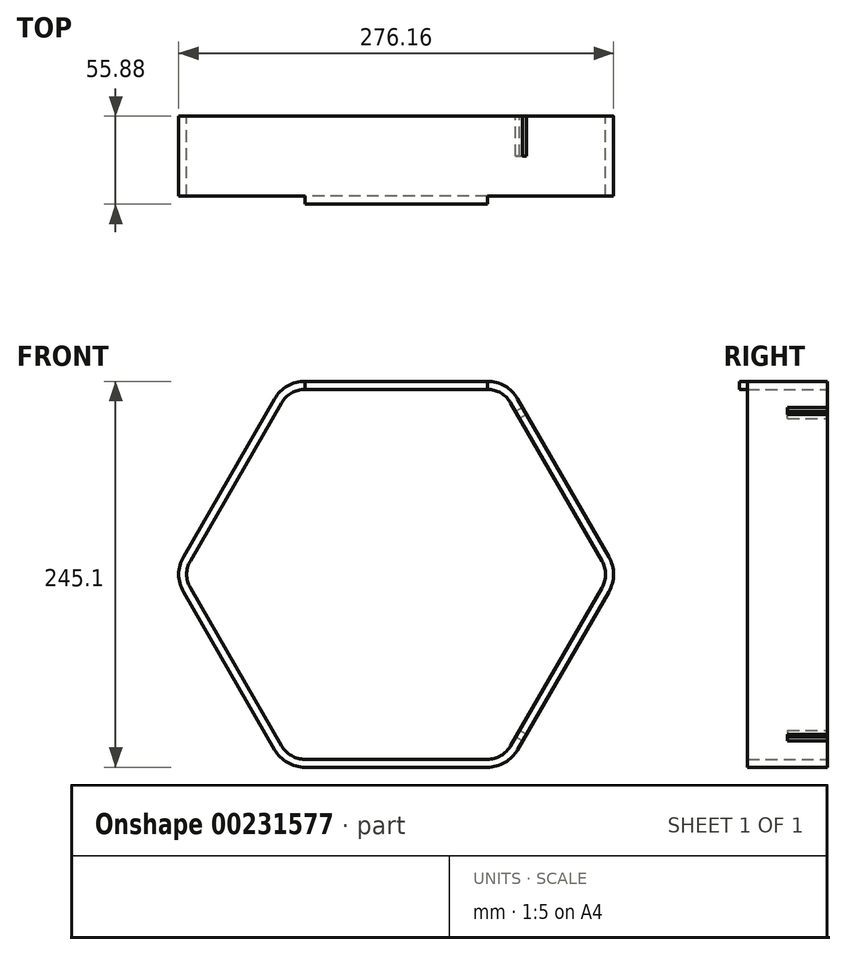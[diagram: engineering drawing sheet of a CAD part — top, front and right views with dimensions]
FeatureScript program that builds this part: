
annotation { "Feature Type Name" : "Feature", "Feature Type Description" : "" }
export const myFeature = defineFeature(function(context is Context, id is Id, definition is map)
    precondition{}
    {
        {
            var Q0;
            Q0=qCreatedBy(makeId("Front.planeOp"),FACE);
            var sketch = newSketch(context, id + "F0", { "sketchPlane" : qUnion([Q0])});
            skCircle(sketch, "E0.cCircle", {"center": v(0, 0) * mm, "radius": 122.56 * mm, "construction": true});
            skLineSegment(sketch, "E0.0", {"start": v(-57.93, 122.55) * mm, "end": v(57.93, 122.55) * mm});
            skLineSegment(sketch, "E0.1", {"start": v(77.17, 111.44) * mm, "end": v(135.1, 11.11) * mm});
            skLineSegment(sketch, "E0.2", {"start": v(135.1, -11.11) * mm, "end": v(77.17, -111.44) * mm});
            skLineSegment(sketch, "E0.3", {"start": v(57.93, -122.55) * mm, "end": v(-57.93, -122.55) * mm});
            skLineSegment(sketch, "E0.4", {"start": v(-77.17, -111.44) * mm, "end": v(-135.1, -11.11) * mm});
            skLineSegment(sketch, "E0.5", {"start": v(-135.1, 11.11) * mm, "end": v(-77.17, 111.44) * mm});
            skPoint(sketch, "E0.0.midPoint", {"position": v(0, 122.55) * mm});
            skPoint(sketch, "E1.visualSharp", {"position": v(-70.76, 122.55) * mm});
            skArc(sketch, "E1.filletArc", {"start": v(-57.93, 122.56) * mm, "mid": v(-69.04, 119.58) * mm, "end": v(-77.17, 111.44) * mm});
            skPoint(sketch, "E2.visualSharp", {"position": v(70.76, 122.55) * mm});
            skArc(sketch, "E2.filletArc", {"start": v(77.17, 111.44) * mm, "mid": v(69.04, 119.58) * mm, "end": v(57.93, 122.56) * mm});
            skPoint(sketch, "E3.visualSharp", {"position": v(141.51, 0) * mm});
            skArc(sketch, "E3.filletArc", {"start": v(135.1, -11.11) * mm, "mid": v(138.08, 0) * mm, "end": v(135.1, 11.11) * mm});
            skPoint(sketch, "E4.visualSharp", {"position": v(70.76, -122.55) * mm});
            skArc(sketch, "E4.filletArc", {"start": v(57.93, -122.56) * mm, "mid": v(69.04, -119.58) * mm, "end": v(77.17, -111.44) * mm});
            skPoint(sketch, "E5.visualSharp", {"position": v(-70.76, -122.56) * mm});
            skArc(sketch, "E5.filletArc", {"start": v(-77.17, -111.44) * mm, "mid": v(-69.04, -119.58) * mm, "end": v(-57.93, -122.56) * mm});
            skPoint(sketch, "E6.visualSharp", {"position": v(-141.51, 0) * mm});
            skArc(sketch, "E6.filletArc", {"start": v(-135.1, 11.11) * mm, "mid": v(-138.08, 0) * mm, "end": v(-135.1, -11.11) * mm});
            skArc(sketch, "E7.0", {"start": v(-130.7, 8.57) * mm, "mid": v(-133, 0) * mm, "end": v(-130.7, -8.57) * mm});
            skLineSegment(sketch, "E7.1", {"start": v(72.77, 108.9) * mm, "end": v(130.7, 8.57) * mm});
            skArc(sketch, "E7.2", {"start": v(72.77, 108.9) * mm, "mid": v(66.5, 115.18) * mm, "end": v(57.93, 117.48) * mm});
            skLineSegment(sketch, "E7.3", {"start": v(-57.93, 117.48) * mm, "end": v(57.93, 117.48) * mm});
            skArc(sketch, "E7.4", {"start": v(-57.93, 117.48) * mm, "mid": v(-66.5, 115.18) * mm, "end": v(-72.77, 108.9) * mm});
            skArc(sketch, "E7.5", {"start": v(130.7, -8.57) * mm, "mid": v(133, 0) * mm, "end": v(130.7, 8.57) * mm});
            skLineSegment(sketch, "E7.6", {"start": v(-130.7, 8.57) * mm, "end": v(-72.77, 108.9) * mm});
            skLineSegment(sketch, "E7.7", {"start": v(130.7, -8.57) * mm, "end": v(72.77, -108.9) * mm});
            skArc(sketch, "E7.8", {"start": v(57.93, -117.48) * mm, "mid": v(66.5, -115.18) * mm, "end": v(72.77, -108.9) * mm});
            skLineSegment(sketch, "E7.9", {"start": v(57.93, -117.48) * mm, "end": v(-57.93, -117.48) * mm});
            skArc(sketch, "E7.10", {"start": v(-72.77, -108.9) * mm, "mid": v(-66.5, -115.18) * mm, "end": v(-57.93, -117.48) * mm});
            skLineSegment(sketch, "E7.11", {"start": v(-72.77, -108.9) * mm, "end": v(-130.7, -8.57) * mm});
            skSolve(sketch);
        }
        {
            var Q0;
            Q0=qCreatedBy(makeId("Right.planeOp"),FACE);
            var sketch = newSketch(context, id + "F1", { "sketchPlane" : qUnion([Q0])});
            skLineSegment(sketch, "E8", {"start": v(0, 0) * mm, "end": v(-208.93, 0) * mm, "construction": true});
            skSolve(sketch);
        }
        {
            var Q0;
            Q0 = qSketchRegion(id + "F0", true);
            extrude(context, id + "F2", {"entities" : qUnion([Q0]), "depth" : 50.8 * mm});
        }
        {
            var Q0;
            {var subQ0=sQuery(id+"F0.wireOp",EDGE,"E7.3");var subQ1=sQuery(id+"F0.wireOp",EDGE,"E6.filletArc");var subQ2=sQuery(id+"F0.wireOp",EDGE,"E7.6");var subQ3=sQuery(id+"F0.wireOp",EDGE,"E1.filletArc");var subQ4=sQuery(id+"F0.wireOp",EDGE,"E0.0");var subQ5=sQuery(id+"F0.wireOp",EDGE,"E5.filletArc");var subQ6=sQuery(id+"F0.wireOp",EDGE,"E0.3");var subQ7=sQuery(id+"F0.wireOp",EDGE,"E7.4");var subQ8=sQuery(id+"F0.wireOp",EDGE,"E0.4");var subQ9=sQuery(id+"F0.wireOp",EDGE,"E7.9");var subQ10=sQuery(id+"F0.wireOp",EDGE,"E7.10");var subQ15=sQuery(id+"F0.wireOp",EDGE,"E7.0");var subQ16=sQuery(id+"F0.wireOp",EDGE,"E0.5");var subQ17=sQuery(id+"F0.wireOp",EDGE,"E7.11");Q0=makeQuery(id+"Fa0krKHR27F3P75_1.1.F5.boolean.opBoolean","SPLIT",FACE,{"disambiguationData":[TD([makeQuery(id+"F2.opExtrude","SWEPT_FACE",FACE,{"disambiguationData":[OSD([subQ8])]})])],"derivedFrom":makeQuery(id+"F2.opExtrude","CAP_FACE",FACE,{"disambiguationData":[OSD([subQ4,sQuery(id+"F0.wireOp",EDGE,"E0.1"),sQuery(id+"F0.wireOp",EDGE,"E0.2"),subQ6,subQ8,subQ16,subQ3,sQuery(id+"F0.wireOp",EDGE,"E2.filletArc"),sQuery(id+"F0.wireOp",EDGE,"E3.filletArc"),sQuery(id+"F0.wireOp",EDGE,"E4.filletArc"),subQ5,subQ1,subQ15,sQuery(id+"F0.wireOp",EDGE,"E7.1"),sQuery(id+"F0.wireOp",EDGE,"E7.2"),subQ0,subQ7,sQuery(id+"F0.wireOp",EDGE,"E7.5"),subQ2,sQuery(id+"F0.wireOp",EDGE,"E7.7"),sQuery(id+"F0.wireOp",EDGE,"E7.8"),subQ9,subQ10,subQ17])],"isStart":false})});}
            var Q1;
            Q1=makeQuery(id+"F2.opExtrude","CAP_FACE",FACE,{"disambiguationData":[OSD([sQuery(id+"F0.wireOp",EDGE,"E0.0"),sQuery(id+"F0.wireOp",EDGE,"E0.1"),sQuery(id+"F0.wireOp",EDGE,"E0.2"),sQuery(id+"F0.wireOp",EDGE,"E0.3"),sQuery(id+"F0.wireOp",EDGE,"E0.4"),sQuery(id+"F0.wireOp",EDGE,"E0.5"),sQuery(id+"F0.wireOp",EDGE,"E1.filletArc"),sQuery(id+"F0.wireOp",EDGE,"E2.filletArc"),sQuery(id+"F0.wireOp",EDGE,"E3.filletArc"),sQuery(id+"F0.wireOp",EDGE,"E4.filletArc"),sQuery(id+"F0.wireOp",EDGE,"E5.filletArc"),sQuery(id+"F0.wireOp",EDGE,"E6.filletArc"),sQuery(id+"F0.wireOp",EDGE,"E7.0"),sQuery(id+"F0.wireOp",EDGE,"E7.1"),sQuery(id+"F0.wireOp",EDGE,"E7.2"),sQuery(id+"F0.wireOp",EDGE,"E7.3"),sQuery(id+"F0.wireOp",EDGE,"E7.4"),sQuery(id+"F0.wireOp",EDGE,"E7.5"),sQuery(id+"F0.wireOp",EDGE,"E7.6"),sQuery(id+"F0.wireOp",EDGE,"E7.7"),sQuery(id+"F0.wireOp",EDGE,"E7.8"),sQuery(id+"F0.wireOp",EDGE,"E7.9"),sQuery(id+"F0.wireOp",EDGE,"E7.10"),sQuery(id+"F0.wireOp",EDGE,"E7.11")])],"isStart":true});
            cPlane(context, id + "F3", {"entities" : qUnion([Q0, Q1]), "cplaneType" : CPlaneType.MID_PLANE, "offset" : 25.4 * mm, "width" : 152.4 * mm, "height" : 152.4 * mm});
        }
        {
            var Q0;
            Q0=makeQuery(id+"F2.opExtrude","SWEPT_FACE",FACE,{"disambiguationData":[OSD([sQuery(id+"F0.wireOp",EDGE,"E7.3")])]});
            var sketch = newSketch(context, id + "F4", { "sketchPlane" : qUnion([Q0])});
            skLineSegment(sketch, "E9.bottom", {"start": v(-57.93, 50.8) * mm, "end": v(57.93, 50.8) * mm});
            skLineSegment(sketch, "E9.top", {"start": v(-57.93, 55.88) * mm, "end": v(57.93, 55.88) * mm});
            skLineSegment(sketch, "E9.left", {"start": v(-57.93, 50.8) * mm, "end": v(-57.93, 55.88) * mm});
            skLineSegment(sketch, "E9.right", {"start": v(57.93, 50.8) * mm, "end": v(57.93, 55.88) * mm});
            skSolve(sketch);
        }
        {
            var Q0;
            Q0=makeQuery(id+"F4.imprint","IMPRINT",FACE,{"disambiguationData":[TD([[makeQuery(id+"F4.imprint","IMPRINT",EDGE,{"derivedFrom":sQuery(id+"F4.wireOp",EDGE,"E9.bottom")}),1.0]])]});
            extrude(context, id + "F5", {"entities" : qUnion([Q0]), "operationType" : NewBodyOperationType.ADD, "oppositeDirection" : true, "depth" : 5.08 * mm});
        }
        {
            var Q0;
            {var subQ0=sQuery(id+"F4.wireOp",EDGE,"E9.right");var subQ1=sQuery(id+"F4.wireOp",EDGE,"E9.left");var subQ2=sQuery(id+"F4.wireOp",EDGE,"E9.top");var subQ3=sQuery(id+"F4.wireOp",EDGE,"E9.bottom");Q0=makeQuery(id+"FPJwFi7Axykp30j_1.1.FVFpjcsYacs48e6_1.4.F5.boolean.opBoolean","MERGE",FACE,{"derivedFrom":[makeQuery(id+"FVFpjcsYacs48e6_1.4.F5.boolean.opBoolean","MERGE",FACE,{"derivedFrom":[makeQuery(id+"F2.opExtrude","SWEPT_FACE",FACE,{"disambiguationData":[OSD([sQuery(id+"F0.wireOp",EDGE,"E0.2")])]}),makeQuery(id+"FVFpjcsYacs48e6_1.4.F5.opExtrude","CAP_FACE",FACE,{"disambiguationData":[OSD([subQ3,subQ2,subQ1,subQ0])],"isStart":false})]}),makeQuery(id+"FPJwFi7Axykp30j_1.1.FVFpjcsYacs48e6_1.4.F5.opExtrude","CAP_FACE",FACE,{"disambiguationData":[OSD([subQ3,subQ2,subQ1,subQ0])],"isStart":false})]});}
            var sketch = newSketch(context, id + "F6", { "sketchPlane" : qUnion([Q0])});
            skLineSegment(sketch, "E10.bottom", {"start": v(5.08, -51.58) * mm, "end": v(-25.4, -51.58) * mm});
            skLineSegment(sketch, "E10.top", {"start": v(5.08, -46.5) * mm, "end": v(-25.4, -46.5) * mm});
            skLineSegment(sketch, "E10.left", {"start": v(5.08, -51.58) * mm, "end": v(5.08, -46.5) * mm});
            skLineSegment(sketch, "E10.right", {"start": v(-25.4, -51.58) * mm, "end": v(-25.4, -46.5) * mm});
            skSolve(sketch);
        }
        {
            var Q0;
            Q0=makeQuery(id+"F6.imprint","IMPRINT",FACE,{"disambiguationData":[TD([[makeQuery(id+"F6.imprint","IMPRINT",EDGE,{"derivedFrom":sQuery(id+"F6.wireOp",EDGE,"E10.bottom")}),-1.0]])]});
            var Q1;
            {var subQ0=sQuery(id+"F4.wireOp",EDGE,"E9.right");var subQ1=sQuery(id+"F4.wireOp",EDGE,"E9.left");var subQ2=sQuery(id+"F4.wireOp",EDGE,"E9.top");var subQ3=sQuery(id+"F4.wireOp",EDGE,"E9.bottom");Q1=makeQuery(id+"FPJwFi7Axykp30j_1.1.FVFpjcsYacs48e6_1.4.F5.boolean.opBoolean","MERGE",FACE,{"derivedFrom":[makeQuery(id+"FVFpjcsYacs48e6_1.4.F5.boolean.opBoolean","MERGE",FACE,{"derivedFrom":[makeQuery(id+"F2.opExtrude","SWEPT_FACE",FACE,{"disambiguationData":[OSD([sQuery(id+"F0.wireOp",EDGE,"E7.7")])]}),makeQuery(id+"FVFpjcsYacs48e6_1.4.F5.opExtrude","CAP_FACE",FACE,{"disambiguationData":[OSD([subQ3,subQ2,subQ1,subQ0])],"isStart":true})]}),makeQuery(id+"FPJwFi7Axykp30j_1.1.FVFpjcsYacs48e6_1.4.F5.opExtrude","CAP_FACE",FACE,{"disambiguationData":[OSD([subQ3,subQ2,subQ1,subQ0])],"isStart":true})]});}
            extrude(context, id + "F7", {"entities" : qUnion([Q0]), "operationType" : NewBodyOperationType.REMOVE, "endBound" : BoundingType.UP_TO_SURFACE, "oppositeDirection" : true, "endBoundEntityFace" : qUnion([Q1]), "depth" : 25.4 * mm});
        }
        {
            var Q0;
            {var subQ0=sQuery(id+"F4.wireOp",EDGE,"E9.right");var subQ1=sQuery(id+"F4.wireOp",EDGE,"E9.left");var subQ2=sQuery(id+"F4.wireOp",EDGE,"E9.top");var subQ3=sQuery(id+"F4.wireOp",EDGE,"E9.bottom");Q0=makeQuery(id+"FPJwFi7Axykp30j_1.1.FVFpjcsYacs48e6_1.5.F5.boolean.opBoolean","MERGE",FACE,{"derivedFrom":[makeQuery(id+"FVFpjcsYacs48e6_1.5.F5.boolean.opBoolean","MERGE",FACE,{"derivedFrom":[makeQuery(id+"F2.opExtrude","SWEPT_FACE",FACE,{"disambiguationData":[OSD([sQuery(id+"F0.wireOp",EDGE,"E0.1")])]}),makeQuery(id+"FVFpjcsYacs48e6_1.5.F5.opExtrude","CAP_FACE",FACE,{"disambiguationData":[OSD([subQ3,subQ2,subQ1,subQ0])],"isStart":false})]}),makeQuery(id+"FPJwFi7Axykp30j_1.1.FVFpjcsYacs48e6_1.5.F5.opExtrude","CAP_FACE",FACE,{"disambiguationData":[OSD([subQ3,subQ2,subQ1,subQ0])],"isStart":false})]});}
            var sketch = newSketch(context, id + "F8", { "sketchPlane" : qUnion([Q0])});
            skLineSegment(sketch, "E11.bottom", {"start": v(5.08, 51.58) * mm, "end": v(-25.4, 51.58) * mm});
            skLineSegment(sketch, "E11.top", {"start": v(5.08, 46.5) * mm, "end": v(-25.4, 46.5) * mm});
            skLineSegment(sketch, "E11.left", {"start": v(5.08, 51.58) * mm, "end": v(5.08, 46.5) * mm});
            skLineSegment(sketch, "E11.right", {"start": v(-25.4, 51.58) * mm, "end": v(-25.4, 46.5) * mm});
            skSolve(sketch);
        }
        {
            var Q0;
            Q0 = qSketchRegion(id + "F8", true);
            var Q1;
            {var subQ0=sQuery(id+"F4.wireOp",EDGE,"E9.right");var subQ1=sQuery(id+"F4.wireOp",EDGE,"E9.left");var subQ2=sQuery(id+"F4.wireOp",EDGE,"E9.top");var subQ3=sQuery(id+"F4.wireOp",EDGE,"E9.bottom");Q1=makeQuery(id+"FPJwFi7Axykp30j_1.1.FVFpjcsYacs48e6_1.5.F5.boolean.opBoolean","MERGE",FACE,{"derivedFrom":[makeQuery(id+"FVFpjcsYacs48e6_1.5.F5.boolean.opBoolean","MERGE",FACE,{"derivedFrom":[makeQuery(id+"F2.opExtrude","SWEPT_FACE",FACE,{"disambiguationData":[OSD([sQuery(id+"F0.wireOp",EDGE,"E7.1")])]}),makeQuery(id+"FVFpjcsYacs48e6_1.5.F5.opExtrude","CAP_FACE",FACE,{"disambiguationData":[OSD([subQ3,subQ2,subQ1,subQ0])],"isStart":true})]}),makeQuery(id+"FPJwFi7Axykp30j_1.1.FVFpjcsYacs48e6_1.5.F5.opExtrude","CAP_FACE",FACE,{"disambiguationData":[OSD([subQ3,subQ2,subQ1,subQ0])],"isStart":true})]});}
            extrude(context, id + "F9", {"entities" : qUnion([Q0]), "operationType" : NewBodyOperationType.REMOVE, "endBound" : BoundingType.UP_TO_SURFACE, "oppositeDirection" : true, "endBoundEntityFace" : qUnion([Q1]), "depth" : 25.4 * mm});
        }
    });
